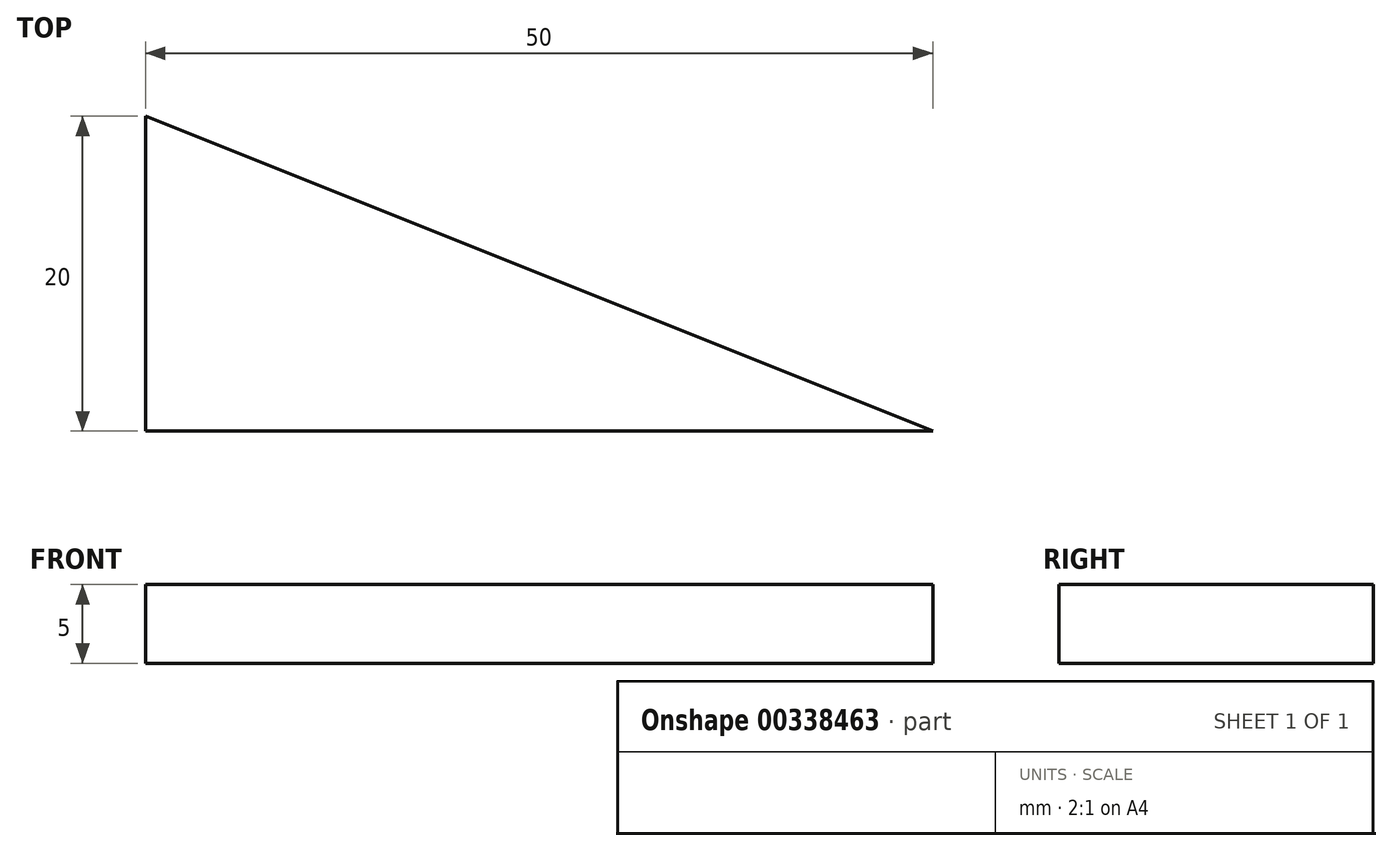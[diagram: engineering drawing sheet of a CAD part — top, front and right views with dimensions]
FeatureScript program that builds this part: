
annotation { "Feature Type Name" : "Feature", "Feature Type Description" : "" }
export const myFeature = defineFeature(function(context is Context, id is Id, definition is map)
    precondition{}
    {
        {
            var Q0;
            Q0=qCreatedBy(makeId("Top.planeOp"),FACE);
            var sketch = newSketch(context, id + "F0", { "sketchPlane" : qUnion([Q0])});
            skLineSegment(sketch, "E0.bottom", {"start": v(0, 0) * mm, "end": v(-50, 0) * mm});
            skLineSegment(sketch, "E0.top", {"start": v(0, 20) * mm, "end": v(-50, 20) * mm});
            skLineSegment(sketch, "E0.left", {"start": v(0, 0) * mm, "end": v(0, 20) * mm});
            skLineSegment(sketch, "E0.right", {"start": v(-50, 0) * mm, "end": v(-50, 20) * mm});
            skLineSegment(sketch, "E1", {"start": v(-50, 20) * mm, "end": v(0, 0) * mm});
            skSolve(sketch);
        }
        {
            var Q0;
            Q0=makeQuery(id+"F0.imprint","IMPRINT",FACE,{"disambiguationData":[TD([[makeQuery(id+"F0.imprint","IMPRINT",EDGE,{"derivedFrom":sQuery(id+"F0.wireOp",EDGE,"E0.bottom")}),-1.0]])]});
            extrude(context, id + "F1", {"entities" : qUnion([Q0]), "depth" : 5 * mm, "offsetDistance" : 25 * mm});
        }
    });
